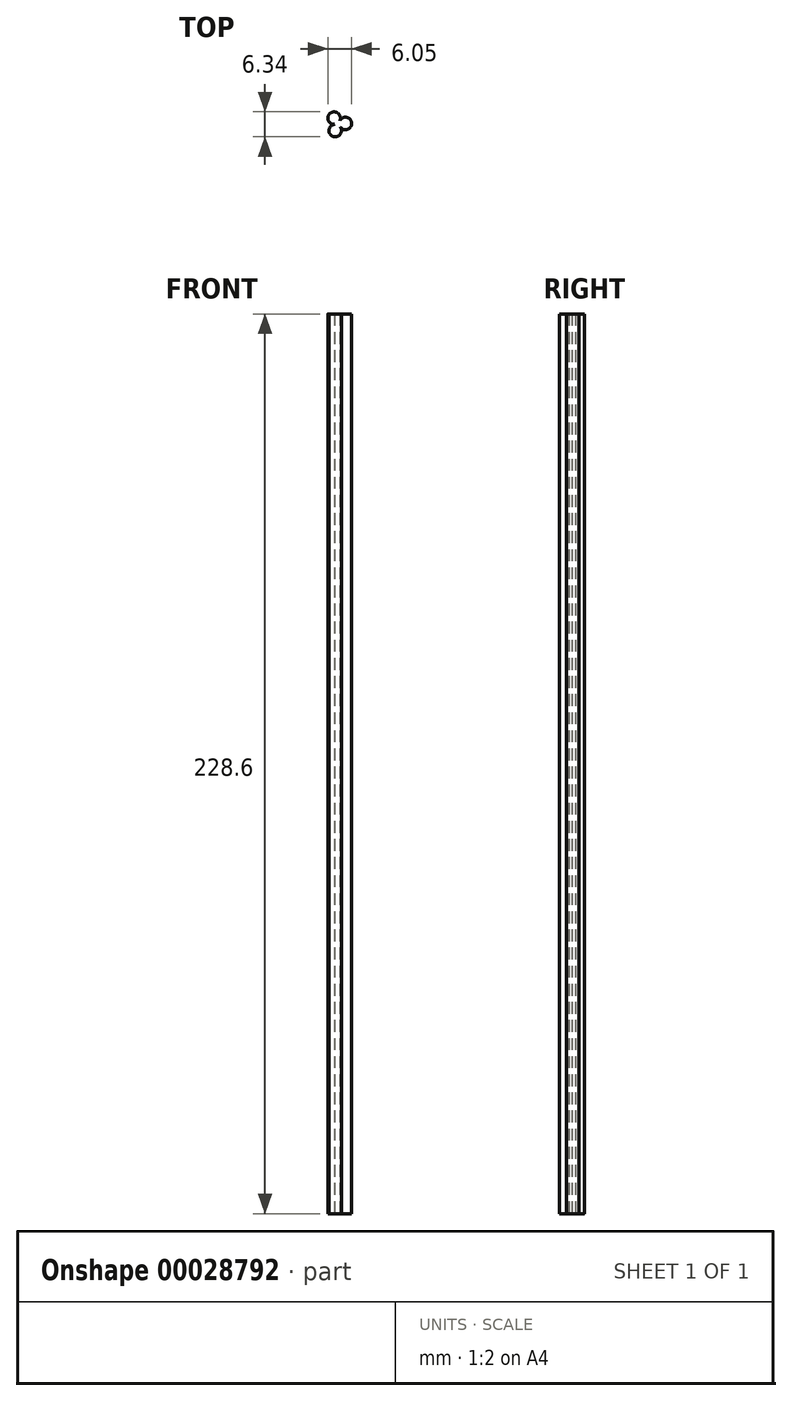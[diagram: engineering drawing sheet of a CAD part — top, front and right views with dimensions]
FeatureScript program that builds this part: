
annotation { "Feature Type Name" : "Feature", "Feature Type Description" : "" }
export const myFeature = defineFeature(function(context is Context, id is Id, definition is map)
    precondition{}
    {
        {
            var Q0;
            Q0=qCreatedBy(makeId("Top.planeOp"),FACE);
            var sketch = newSketch(context, id + "F0", { "sketchPlane" : qUnion([Q0])});
            skCircle(sketch, "E0", {"center": v(0, 0) * mm, "radius": 1.59 * mm});
            skCircle(sketch, "E1", {"center": v(-2.87, 1.36) * mm, "radius": 1.59 * mm});
            skCircle(sketch, "E2", {"center": v(-2.61, -1.8) * mm, "radius": 1.59 * mm});
            skSolve(sketch);
        }
        {
            var Q0;
            {var subQ1=sQuery(id+"F0.wireOp",EDGE,"E1");var subQ3=sQuery(id+"F0.wireOp",EDGE,"E0");var subQ5=makeQuery(id+"F0.imprint","INTERSECT",VERTEX,{"derivedFrom":[subQ3,subQ1]});Q0=makeQuery(id+"F0.imprint","IMPRINT",FACE,{"disambiguationData":[TD([[makeQuery(id+"F0.imprint","IMPRINT",EDGE,{"disambiguationData":[TD([[subQ5,-1.0]])],"derivedFrom":subQ3}),-1.0]])]});}
            var Q1;
            {var subQ0=sQuery(id+"F0.wireOp",EDGE,"E1");var subQ2=makeQuery(id+"F0.imprint","INTERSECT",VERTEX,{"derivedFrom":[sQuery(id+"F0.wireOp",EDGE,"E0"),subQ0]});Q1=makeQuery(id+"F0.imprint","IMPRINT",FACE,{"disambiguationData":[TD([[makeQuery(id+"F0.imprint","IMPRINT",EDGE,{"disambiguationData":[TD([[subQ2,1.0]])],"derivedFrom":subQ0}),1.0]])]});}
            var Q2;
            {var subQ0=sQuery(id+"F0.wireOp",EDGE,"E2");var subQ2=makeQuery(id+"F0.imprint","INTERSECT",VERTEX,{"derivedFrom":[sQuery(id+"F0.wireOp",EDGE,"E0"),subQ0]});Q2=makeQuery(id+"F0.imprint","IMPRINT",FACE,{"disambiguationData":[TD([[makeQuery(id+"F0.imprint","IMPRINT",EDGE,{"disambiguationData":[TD([[subQ2,-1.0]])],"derivedFrom":subQ0}),1.0]])]});}
            var Q3;
            {var subQ0=sQuery(id+"F0.wireOp",EDGE,"E0");var subQ2=makeQuery(id+"F0.imprint","INTERSECT",VERTEX,{"derivedFrom":[subQ0,sQuery(id+"F0.wireOp",EDGE,"E1")]});Q3=makeQuery(id+"F0.imprint","IMPRINT",FACE,{"disambiguationData":[TD([[makeQuery(id+"F0.imprint","IMPRINT",EDGE,{"disambiguationData":[TD([[subQ2,-1.0]])],"derivedFrom":subQ0}),1.0]])]});}
            extrude(context, id + "F1", {"entities" : qUnion([Q0, Q1, Q2, Q3]), "depth" : 228.6 * mm});
        }
    });
